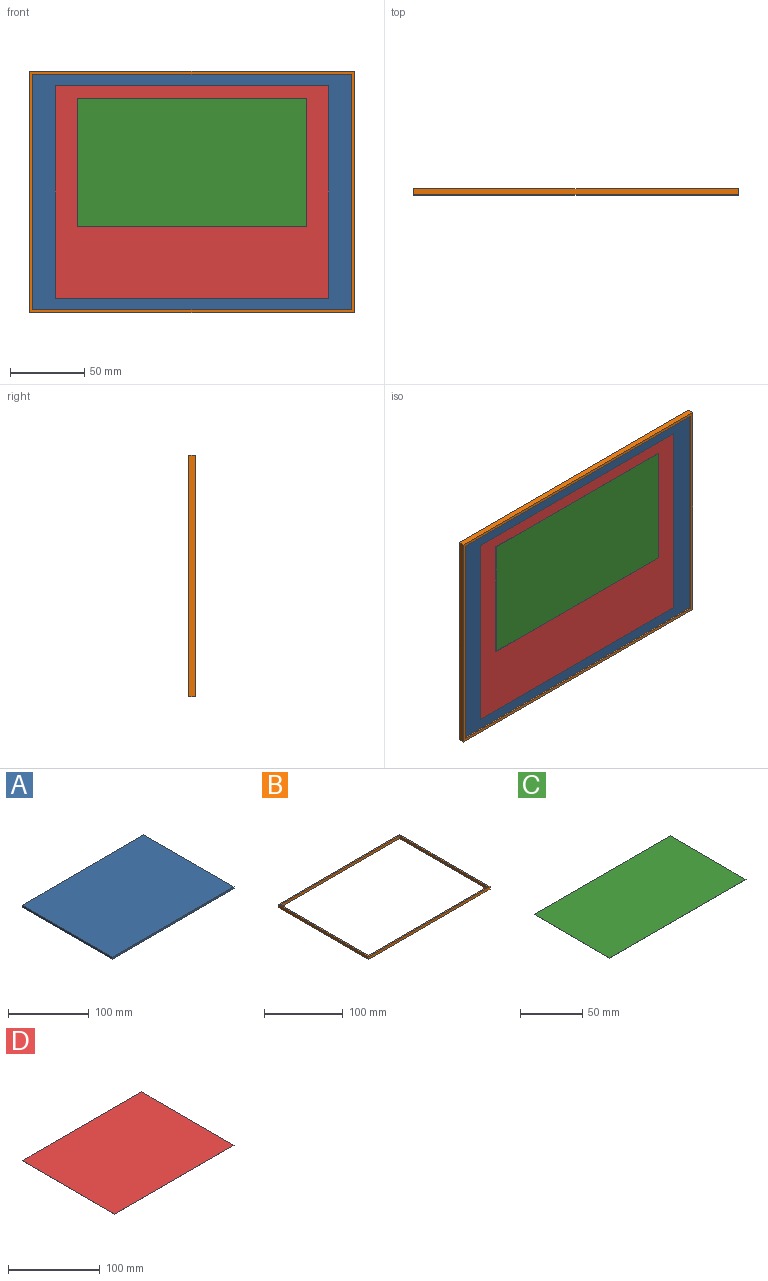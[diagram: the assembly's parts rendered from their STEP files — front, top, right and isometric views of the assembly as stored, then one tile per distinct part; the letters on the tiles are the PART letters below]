
ASSEMBLY  parts=4 mates=3
PART A: 6 faces, bbox 214x158x3 mm
  f0: plane 158x3mm, normal (1,0,0), area 474mm2, adj f1,f2,f3,f5
  f1: plane 214x158mm, normal (0,0,-1), area 33812mm2, adj f0,f2,f3,f4
  f2: plane 214x3mm, normal (0,1,0), area 642mm2, adj f0,f1,f4,f5
  f3: plane 214x3mm, normal (0,-1,0), area 642mm2, adj f0,f1,f4,f5
  f4: plane 158x3mm, normal (-1,0,0), area 474mm2, adj f1,f2,f3,f5
  f5: plane 214x158mm, normal (0,0,1), area 33812mm2, adj f0,f2,f3,f4
PART B: 10 faces, bbox 218x162x4.2 mm
  f0: plane 158x4.2mm, normal (-1,0,0), area 663.6mm2, adj f1,f2,f7,f8
  f1: plane 214x4.2mm, normal (0,-1,0), area 898.8mm2, adj f0,f7,f8,f9
  f2: plane 214x4.2mm, normal (0,1,0), area 898.8mm2, adj f0,f7,f8,f9
  f3: plane 218x4.2mm, normal (0,-1,0), area 915.6mm2, adj f4,f6,f7,f8
  f4: plane 162x4.2mm, normal (-1,0,0), area 680.4mm2, adj f3,f5,f7,f8
  f5: plane 218x4.2mm, normal (0,1,0), area 915.6mm2, adj f4,f6,f7,f8
  f6: plane 162x4.2mm, normal (1,0,0), area 680.4mm2, adj f3,f5,f7,f8
  f7: plane 218x162mm, normal (0,0,1), area 1504mm2, adj f0,f1,f2,f3,f4,f5,f6,f9
  f8: plane 218x162mm, normal (0,0,-1), area 1504mm2, adj f0,f1,f2,f3,f4,f5,f6,f9
  f9: plane 158x4.2mm, normal (1,0,0), area 663.6mm2, adj f1,f2,f7,f8
PART C: 6 faces, bbox 154x86x0.1 mm
  f0: plane 86x0.1mm, normal (1,0,0), area 8.6mm2, adj f1,f2,f3,f5
  f1: plane 154x86mm, normal (0,0,-1), area 13244mm2, adj f0,f2,f3,f4
  f2: plane 154x0.1mm, normal (0,1,0), area 15.4mm2, adj f0,f1,f4,f5
  f3: plane 154x0.1mm, normal (0,-1,0), area 15.4mm2, adj f0,f1,f4,f5
  f4: plane 86x0.1mm, normal (-1,0,0), area 8.6mm2, adj f1,f2,f3,f5
  f5: plane 154x86mm, normal (0,0,1), area 13244mm2, adj f0,f2,f3,f4
PART D: 6 faces, bbox 184x143x0.1 mm
  f0: plane 143x0.1mm, normal (1,0,0), area 14.3mm2, adj f1,f2,f3,f5
  f1: plane 184x143mm, normal (0,0,-1), area 26312mm2, adj f0,f2,f3,f4
  f2: plane 184x0.1mm, normal (0,1,0), area 18.4mm2, adj f0,f1,f4,f5
  f3: plane 184x0.1mm, normal (0,-1,0), area 18.4mm2, adj f0,f1,f4,f5
  f4: plane 143x0.1mm, normal (-1,0,0), area 14.3mm2, adj f1,f2,f3,f5
  f5: plane 184x143mm, normal (0,0,1), area 26312mm2, adj f0,f2,f3,f4
PLACE A rot(axis=(-1,0,0),90deg) t=(-141.91,-291.66,437.88)mm
PLACE B rot(axis=(-1,0,0),90deg) t=(-141.91,-291.66,437.88)mm
PLACE C rot(axis=(-1,0,0),90deg) t=(-141.91,-294.76,457.88)mm
PLACE D rot(axis=(1,0,0),90deg) t=(-141.91,-294.76,437.88)mm
MATE fastened C.f5 <-> D.f5  axis (0,1,0) through (-141.91,-294.76,457.88)mm
MATE fastened A.f5 <-> B.f7  axis (0,1,0) through (-34.91,-291.66,437.88)mm
MATE fastened D.f1 <-> A.f1  axis (0,1,0) through (-141.91,-294.66,437.88)mm
